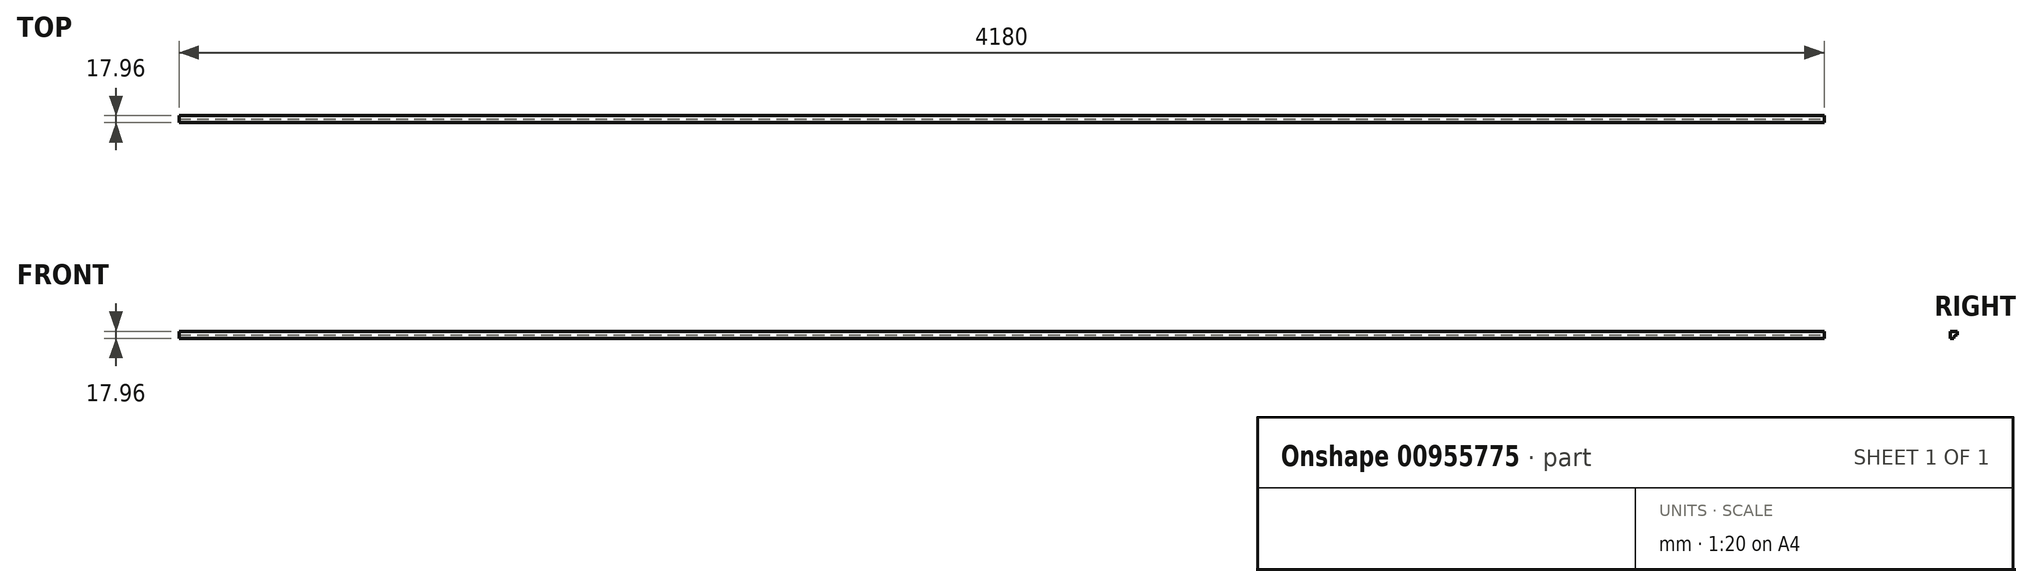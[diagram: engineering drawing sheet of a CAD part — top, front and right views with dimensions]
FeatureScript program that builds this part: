
annotation { "Feature Type Name" : "Feature", "Feature Type Description" : "" }
export const myFeature = defineFeature(function(context is Context, id is Id, definition is map)
    precondition{}
    {
        {
            var Q0;
            Q0=qCreatedBy(makeId("Right.planeOp"),FACE);
            var sketch = newSketch(context, id + "F0", { "sketchPlane" : qUnion([Q0])});
            skLineSegment(sketch, "E0.bottom", {"start": v(-0.95, 3.56) * mm, "end": v(17.01, 3.56) * mm});
            skLineSegment(sketch, "E0.top", {"start": v(-0.95, -14.4) * mm, "end": v(17.01, -14.4) * mm});
            skLineSegment(sketch, "E0.left", {"start": v(-0.95, 3.56) * mm, "end": v(-0.95, -14.4) * mm});
            skLineSegment(sketch, "E0.right", {"start": v(17.01, 3.56) * mm, "end": v(17.01, -14.4) * mm});
            skPoint(sketch, "E0.middle", {"position": v(8.03, -5.42) * mm});
            skLineSegment(sketch, "E1", {"start": v(8.03, -5.42) * mm, "end": v(17.01, -5.42) * mm});
            skCircle(sketch, "E2", {"center": v(17.01, -14.4) * mm, "radius": 8.98 * mm});
            skSolve(sketch);
        }
        {
            var Q0;
            {var subQ1=sQuery(id+"F0.wireOp",EDGE,"E0.bottom");Q0=makeQuery(id+"F0.imprint","IMPRINT",FACE,{"disambiguationData":[TD([[makeQuery(id+"F0.imprint","IMPRINT",EDGE,{"derivedFrom":subQ1}),-1.0]])]});}
            extrude(context, id + "F1", {"entities" : qUnion([Q0]), "oppositeDirection" : true, "depth" : 4180 * mm, "offsetDistance" : 25.4 * mm});
        }
    });
